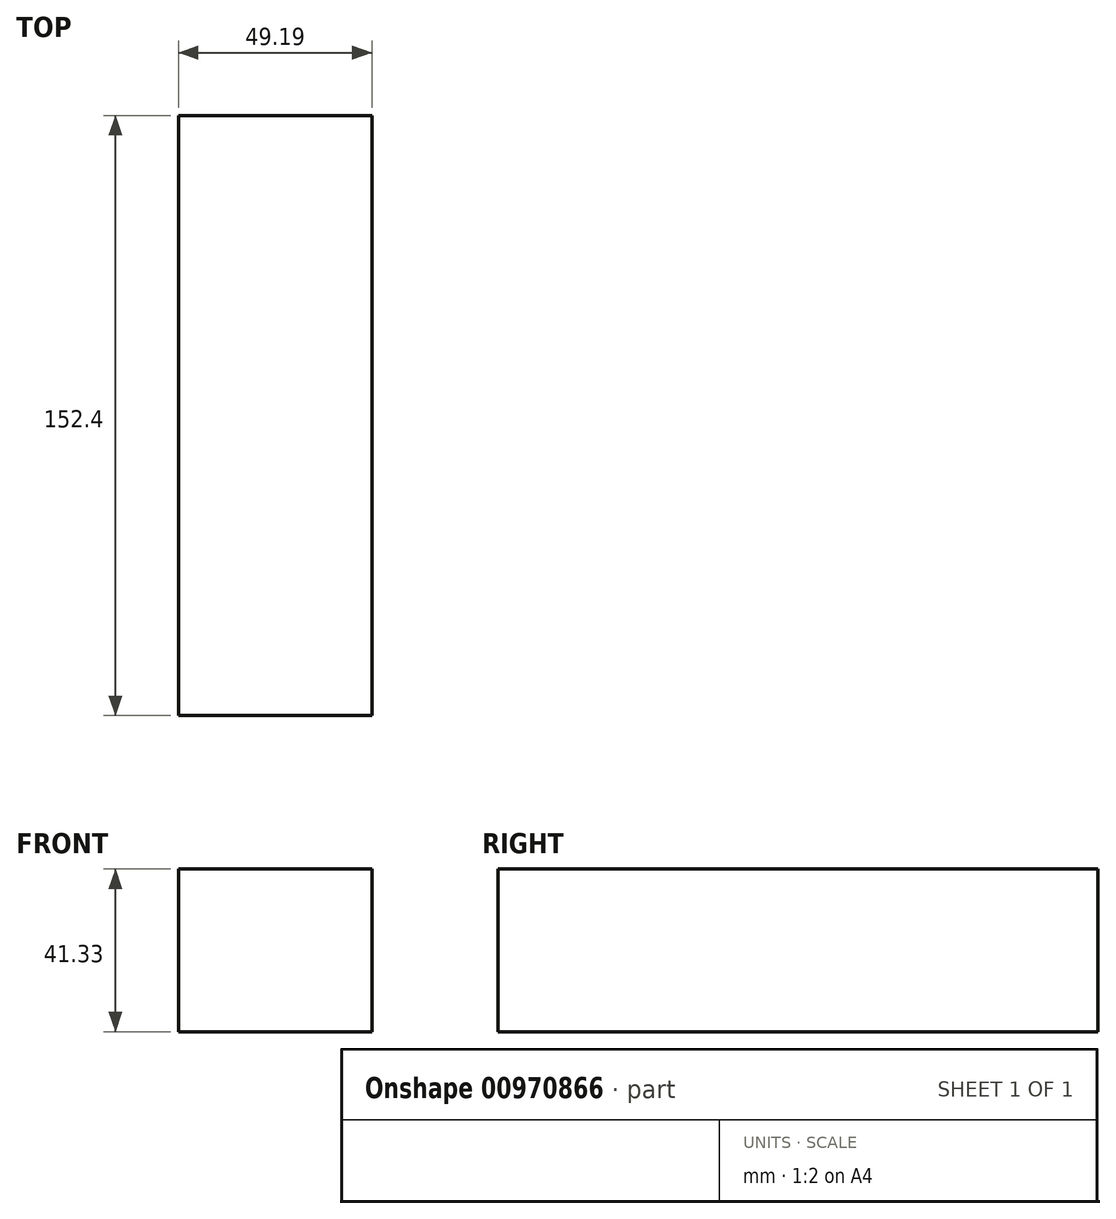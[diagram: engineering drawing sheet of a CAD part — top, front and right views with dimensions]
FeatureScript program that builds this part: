
annotation { "Feature Type Name" : "Feature", "Feature Type Description" : "" }
export const myFeature = defineFeature(function(context is Context, id is Id, definition is map)
    precondition{}
    {
        {
            var Q0;
            Q0=qCreatedBy(makeId("Front.planeOp"),FACE);
            var sketch = newSketch(context, id + "F0", { "sketchPlane" : qUnion([Q0])});
            skLineSegment(sketch, "E0.bottom", {"start": v(-279.58, -17.1) * mm, "end": v(-230.39, -17.1) * mm});
            skLineSegment(sketch, "E0.top", {"start": v(-279.58, -33.03) * mm, "end": v(-230.39, -33.03) * mm});
            skLineSegment(sketch, "E0.left", {"start": v(-279.58, -17.1) * mm, "end": v(-279.58, -33.03) * mm});
            skLineSegment(sketch, "E0.right", {"start": v(-230.39, -17.1) * mm, "end": v(-230.39, -33.03) * mm});
            skSolve(sketch);
        }
        {
            var Q0;
            Q0=qCreatedBy(makeId("Front.planeOp"),FACE);
            var sketch = newSketch(context, id + "F1", { "sketchPlane" : qUnion([Q0])});
            skSolve(sketch);
        }
        {
            var Q0;
            Q0 = qSketchRegion(id + "F1", true);
            var Q1;
            Q1=makeQuery(id+"F0.imprint","IMPRINT",FACE,{"disambiguationData":[TD([[makeQuery(id+"F0.imprint","IMPRINT",EDGE,{"derivedFrom":sQuery(id+"F0.wireOp",EDGE,"E0.bottom")}),-1.0]])]});
            extrude(context, id + "F2", {"entities" : qUnion([Q0, Q1]), "depth" : 152.4 * mm, "offsetDistance" : 25.4 * mm, "symmetric" : true});
        }
        {
            var Q0;
            Q0=makeQuery(id+"F2.opExtrude","SWEPT_FACE",FACE,{"disambiguationData":[OSD([sQuery(id+"F0.wireOp",EDGE,"E0.bottom")])]});
            var sketch = newSketch(context, id + "F3", { "sketchPlane" : qUnion([Q0])});
            skSolve(sketch);
        }
        {
            var Q0;
            {var subQ0=sQuery(id+"F0.wireOp",EDGE,"E0.bottom");Q0=makeQuery(id+"F3.imprint","IMPRINT",FACE,{"disambiguationData":[TD([[makeQuery(id+"F3.imprint","IMPRINT",EDGE,{"derivedFrom":makeQuery(id+"F2.opExtrude","CAP_EDGE",EDGE,{"disambiguationData":[OSD([subQ0])],"isStart":true})}),-1.0]])]});}
            extrude(context, id + "F4", {"entities" : qUnion([Q0]), "operationType" : NewBodyOperationType.ADD, "depth" : 25.4 * mm, "offsetDistance" : 25.4 * mm});
        }
    });
